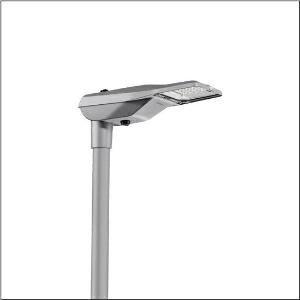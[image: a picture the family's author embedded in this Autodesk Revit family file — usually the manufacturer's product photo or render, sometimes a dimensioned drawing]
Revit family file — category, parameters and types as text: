
# Revit family: streetlight_sl_21_iq_micro___st1_0a_5xe1d51y08db_19c1
name_source: partatom
category: Lighting Fixtures
units: mm (PartAtom-declared; Revit-internal decimal feet)

## family parameters
Cut with Voids When Loaded = No
Host = Face
Light Source = No
Part Type = Normal
Room Calculation Point = No
Round Connector Dimension = Use Diameter
Shared = No

## types (1)
- --- (1 x LED, 4490 lm, 39.1 W, 3000K)
    Apparent Load = 39 VA
    CIE Flux Codes = 37 72 97 100 100
    Color Rendering = 80
    Color Temperature = 3000K
    Default Elevation = 1800 mm
    Description = Streetlight SL 21 iQ micro, mast luminaire, primary light control with lens, of PMMA, primary optical cover: cover, of toughened safety glass, transparent, light distribution: ST1.0a, light emission: direct distribution, primary light characteristic: asymmetric, installation type: post-top, side-entry, LED, High Power LED, rated luminous flux: 4.490lm, luminous efficacy: 115lm/W, light colour: 830, colour temperature: 3000K, control: pre-setting: logarithmic dimming characteristic, Street-Remote, Auto-Match, Temp-Guard, Lumen-Switch, Night-Set, Smart-Wire, Light-Fading, Desk-Remote (wireless, voltage-free reading and setting of iQ features in the workshop via application-optimized NFC function/RFID function), optimised constant luminous flux control (CLO 2.0), mains connection: 220..240V, AC, 50/60Hz, start of lifetime: 39W, end of service life: 41W, reduction: 17W, luminaire housing, of diecast aluminium, powder-coated, Siteco® metallic grey (DB 702S), corrosivity category C5 mid according to DIN EN ISO 12944, please order mast flange separately, inclination adjustable: 0°, 5°, 10°, 15°, sealing non-destructively replaceable, multi-level sealing system, length: 528mm, width: 235mm, height: 110mm, mast flange for spigot size: 42mm (side-entry): 5XC10008XM4, 60/48mm (side-entry/post-top): 5XC10108XM2, 76/60mm (side-entry/post-top): 5XC10108XM1, Smart Interface below and above, protection rating (complete): IP66, insulation class (complete): insulation class II (safety insulation), certification: CE, ENEC, ENEC+, VDE, impact resistance: IK09, permissible operating ambient temperature for outdoor applications: -40..+50°C, standard-compliant lighting for roads and squares, packaging unit: 1 piece

Light Distribution: ST1.0a
    Height = 110 mm
    Lamp = 1 x LED
    Lamp Light Flux = 4490 lm
    Lamp Power = 39.1 W
    Lamp count = 1
    Length = 528 mm
    Luminous efficacy = 115 lm/W
    Manufacturer = Siteco
    ModVariant = No
    Model = 5XE1D51Y08DB
    Number of Poles = 1
    OnlyDefault = Yes
    Power Factor = 1
    Product Name = Streetlight SL 21 iQ micro | ST1.0a
    Product group = mast luminaire | pylon top
    ProductGroupID = 6100
    Protection Class = Protection class II
    Protection Degree = IP 66
    RLX_Detail_Level = 1
    RLX_Emergency_Light_Flux = 0 lm
    RLX_Emergency_Type = 0
    RLX_Emergency_Type_DB = No
    RlxData = <blob elided: 98817 chars, md5=68d7f672>
    Socket = socket
    Standby Power = 0 W
    System Light Flux = 4490 lm
    System Power = 39 W
    Type Comments = factory setting: luminous flux: 100 % | dim-lin: 254 | 765 mA
    Type Image = l_1007239.jpg
    URL = http://relux.com
    VarID = @adj_084189
    Voltage = 0 V
    Weight = 0.00 kg
    Width = 235 mm

## geometry (parser evidence)
native form markers: Blend x4, Sweep x10
no freeform markers — native parametric forms only
